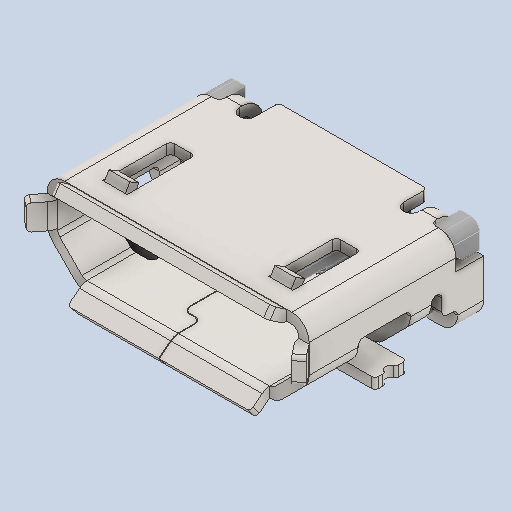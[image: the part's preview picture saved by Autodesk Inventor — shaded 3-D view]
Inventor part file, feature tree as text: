
AUTODESK INVENTOR PART (.ipt)
format: ipt  version: 2023 (Build 270158000, 158)  size: 758,272 bytes
history: native  units: in
note: dims shown in document units (in); Inventor stores cm internally (conversion verified against a paired STEP export)
features: other x11, fillet x2, chamfer x1
ambient origin geometry x8: Origin, YZ Plane, XZ Plane, XY Plane, X Axis, Y Axis, Z Axis, Center Point
bodies: Body1 (feature_tree), Body2 (feature_tree), Body3 (feature_tree), Body4 (feature_tree), Body5 (feature_tree), Body6 (feature_tree), Body7 (feature_tree)
feature tree (14):
  other  "Bryła1"
  other  "Bryła2"
  other  "Bryła3"
  other  "Bryła4"
  other  "Bryła5"
  other  "Bryła6"
  other  "Bryła7"
  fillet  "Fillet2"  [1 undecoded]
  fillet  "Fillet6"  [1 undecoded]
  chamfer  "Chamfer6"  [1 undecoded]
  other  "LPattern5[1]"
  other  "LPattern5[2]"
  other  "LPattern6[1]"
  other  "LPattern6[2]"
note: 3 required parameter values undecoded (feature->parameter linkage not recoverable at this tier; creation-order binding heuristic only, values carry confidence <= 0.55)
